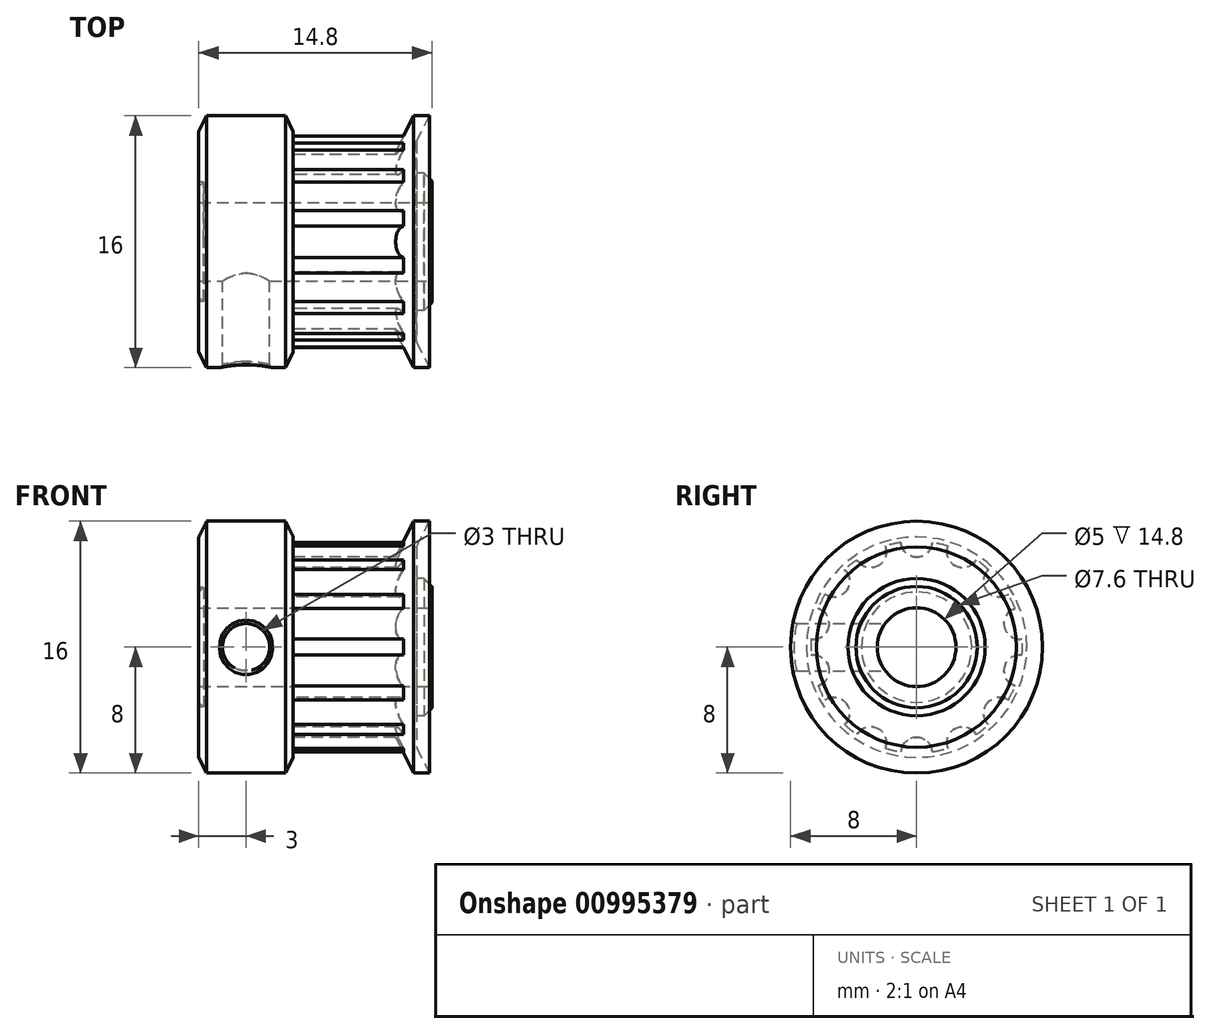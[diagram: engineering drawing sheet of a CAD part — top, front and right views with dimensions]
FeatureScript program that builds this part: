
annotation { "Feature Type Name" : "Feature", "Feature Type Description" : "" }
export const myFeature = defineFeature(function(context is Context, id is Id, definition is map)
    precondition{}
    {
        {
            var Q0;
            Q0=qCreatedBy(makeId("Front.planeOp"),FACE);
            var sketch = newSketch(context, id + "F0", { "sketchPlane" : qUnion([Q0])});
            skLineSegment(sketch, "E0", {"start": v(0, 7) * mm, "end": v(0, 3.8) * mm, "construction": true});
            skLineSegment(sketch, "E1", {"start": v(0, 0) * mm, "end": v(14.8, 0) * mm, "construction": true});
            skLineSegment(sketch, "E2", {"start": v(0, 7) * mm, "end": v(0, 3.9) * mm});
            skLineSegment(sketch, "E3", {"start": v(0.5, 8) * mm, "end": v(5.5, 8) * mm});
            skLineSegment(sketch, "E4", {"start": v(5.5, 8) * mm, "end": v(6, 7) * mm});
            skLineSegment(sketch, "E5", {"start": v(6, 7) * mm, "end": v(6, 6.72) * mm});
            skLineSegment(sketch, "E6", {"start": v(6, 6.72) * mm, "end": v(13, 6.72) * mm});
            skLineSegment(sketch, "E7", {"start": v(13, 6.72) * mm, "end": v(13.64, 8) * mm});
            skLineSegment(sketch, "E8", {"start": v(13.64, 8) * mm, "end": v(14.64, 8) * mm});
            skPoint(sketch, "E9.endSnap0", {"position": v(14.14, 8) * mm});
            skLineSegment(sketch, "E10", {"start": v(0, 7) * mm, "end": v(0.5, 8) * mm});
            skLineSegment(sketch, "E11", {"start": v(0.1, 3.8) * mm, "end": v(0.3, 3.8) * mm});
            skLineSegment(sketch, "E12", {"start": v(0.3, 3.8) * mm, "end": v(0, 3.5) * mm});
            skLineSegment(sketch, "E13.trimOffspring", {"start": v(0, 3.5) * mm, "end": v(0, 0) * mm, "construction": true});
            skLineSegment(sketch, "E14.trimOffspring", {"start": v(0, 3.5) * mm, "end": v(0, 0) * mm});
            skPoint(sketch, "E15.visualSharp", {"position": v(14.8, 0) * mm});
            skPoint(sketch, "E16.visualSharp", {"position": v(0, 3.8) * mm});
            skArc(sketch, "E16.filletArc", {"start": v(0, 3.9) * mm, "mid": v(0.03, 3.83) * mm, "end": v(0.1, 3.8) * mm});
            skLineSegment(sketch, "E17", {"start": v(13.82, 4.35) * mm, "end": v(14.3, 4.35) * mm});
            skLineSegment(sketch, "E18", {"start": v(14.8, 3.85) * mm, "end": v(14.8, 0) * mm});
            skLineSegment(sketch, "E19", {"start": v(14.3, 4.35) * mm, "end": v(14.8, 3.85) * mm});
            skPoint(sketch, "E20.orphan", {"position": v(14.8, 4.35) * mm});
            skLineSegment(sketch, "E21", {"start": v(14.64, 8) * mm, "end": v(13.82, 6.35) * mm});
            skLineSegment(sketch, "E22", {"start": v(13.82, 6.35) * mm, "end": v(13.82, 4.35) * mm});
            skPoint(sketch, "E23.orphan", {"position": v(14.14, 4.35) * mm});
            skLineSegment(sketch, "E24", {"start": v(0, 0) * mm, "end": v(14.8, 0) * mm});
            skSolve(sketch);
        }
        {
            var Q0;
            Q0 = qSketchRegion(id + "F0", true);
            var Q1;
            Q1=sQuery(id+"F0.wireOp",EDGE,"E24");
            revolve(context, id + "F1", {"surfaceOperationType" : NewSurfaceOperationType.NEW, "entities" : qUnion([Q0]), "axis" : qUnion([Q1]), "revolveType" : RevolveType.FULL});
        }
        {
            var Q0;
            Q0=makeQuery(id+"F1.opRevolve","SWEPT_FACE",FACE,{"disambiguationData":[OSD([sQuery(id+"F0.wireOp",EDGE,"E18")])]});
            var sketch = newSketch(context, id + "F2", { "sketchPlane" : qUnion([Q0])});
            skSolve(sketch);
        }
        {
            var Q0;
            Q0=makeQuery(id+"F2.imprint","IMPRINT",FACE,{"disambiguationData":[TD([[makeQuery(id+"F2.imprint","IMPRINT",EDGE,{"derivedFrom":makeQuery(id+"F1.opRevolve","SWEPT_EDGE",EDGE,{"disambiguationData":[OSD([sQuery(id+"F0.wireOp",EDGE,"E18"),sQuery(id+"F0.wireOp",EDGE,"E19")])]})}),-1.0]])]});
            var sketch = newSketch(context, id + "F3", { "sketchPlane" : qUnion([Q0])});
            skCircle(sketch, "E25", {"center": v(0, 0) * mm, "radius": 2.5 * mm});
            skSolve(sketch);
        }
        {
            var Q0;
            Q0 = qSketchRegion(id + "F3", true);
            extrude(context, id + "F4", {"entities" : qUnion([Q0]), "operationType" : NewBodyOperationType.REMOVE, "endBound" : BoundingType.THROUGH_ALL, "oppositeDirection" : true, "depth" : 25 * mm, "offsetDistance" : 25 * mm});
        }
        {
            var Q0;
            Q0=makeQuery(id+"F1.opRevolve","SWEPT_FACE",FACE,{"disambiguationData":[OSD([sQuery(id+"F0.wireOp",EDGE,"E5")])]});
            var sketch = newSketch(context, id + "F5", { "sketchPlane" : qUnion([Q0])});
            skLineSegment(sketch, "E26", {"start": v(0, 0) * mm, "end": v(0, 6.72) * mm, "construction": true});
            skSolve(sketch);
        }
        {
            var Q0;
            {var subQ0=sQuery(id+"F0.wireOp",EDGE,"E5");Q0=makeQuery(id+"F5.imprint","IMPRINT",FACE,{"disambiguationData":[TD([[makeQuery(id+"F5.imprint","IMPRINT",EDGE,{"derivedFrom":makeQuery(id+"F1.opRevolve","SWEPT_EDGE",EDGE,{"disambiguationData":[OSD([sQuery(id+"F0.wireOp",EDGE,"E4"),subQ0])]})}),-1.0]])]});}
            var sketch = newSketch(context, id + "F6", { "sketchPlane" : qUnion([Q0])});
            skCircle(sketch, "E27", {"center": v(0, 6.72) * mm, "radius": 1 * mm});
            skCircle(sketch, "E28.1.0", {"center": v(-2.92, 6.05) * mm, "radius": 1 * mm});
            skCircle(sketch, "E28.2.0", {"center": v(-5.25, 4.19) * mm, "radius": 1 * mm});
            skCircle(sketch, "E28.3.0", {"center": v(-6.55, 1.5) * mm, "radius": 1 * mm});
            skCircle(sketch, "E28.4.0", {"center": v(-6.55, -1.5) * mm, "radius": 1 * mm});
            skCircle(sketch, "E28.5.0", {"center": v(-5.25, -4.19) * mm, "radius": 1 * mm});
            skCircle(sketch, "E28.6.0", {"center": v(-2.92, -6.05) * mm, "radius": 1 * mm});
            skCircle(sketch, "E28.7.0", {"center": v(0, -6.72) * mm, "radius": 1 * mm});
            skCircle(sketch, "E28.8.0", {"center": v(2.92, -6.05) * mm, "radius": 1 * mm});
            skCircle(sketch, "E28.9.0", {"center": v(5.25, -4.19) * mm, "radius": 1 * mm});
            skCircle(sketch, "E28.10.0", {"center": v(6.55, -1.5) * mm, "radius": 1 * mm});
            skCircle(sketch, "E28.11.0", {"center": v(6.55, 1.5) * mm, "radius": 1 * mm});
            skCircle(sketch, "E28.12.0", {"center": v(5.25, 4.19) * mm, "radius": 1 * mm});
            skCircle(sketch, "E28.13.0", {"center": v(2.92, 6.05) * mm, "radius": 1 * mm});
            skPoint(sketch, "E28.center", {"position": v(0, 0) * mm});
            skSolve(sketch);
        }
        {
            var Q0;
            Q0 = qSketchRegion(id + "F6", true);
            var Q1;
            Q1=makeQuery(id+"F1.opRevolve","SWEPT_FACE",FACE,{"disambiguationData":[OSD([sQuery(id+"F0.wireOp",EDGE,"E7")])]});
            extrude(context, id + "F7", {"entities" : qUnion([Q0]), "operationType" : NewBodyOperationType.REMOVE, "endBound" : BoundingType.UP_TO_SURFACE, "depth" : 25 * mm, "endBoundEntityFace" : qUnion([Q1]), "offsetDistance" : 25 * mm});
        }
        {
            var Q0;
            Q0=qCreatedBy(makeId("Front.planeOp"),FACE);
            var sketch = newSketch(context, id + "F8", { "sketchPlane" : qUnion([Q0])});
            skLineSegment(sketch, "E29", {"start": v(0, 0) * mm, "end": v(6.13, 0) * mm, "construction": true});
            skCircle(sketch, "E30", {"center": v(3, 0) * mm, "radius": 1.5 * mm});
            skSolve(sketch);
        }
        {
            var Q0;
            Q0 = qSketchRegion(id + "F8", true);
            extrude(context, id + "F9", {"entities" : qUnion([Q0]), "operationType" : NewBodyOperationType.REMOVE, "depth" : 25 * mm, "offsetDistance" : 25 * mm});
        }
        {
            var Q0;
            Q0=makeQuery(id+"F9.boolean.opBoolean","INTERSECT",EDGE,{"derivedFrom":[makeQuery(id+"F1.opRevolve","SWEPT_FACE",FACE,{"disambiguationData":[OSD([sQuery(id+"F0.wireOp",EDGE,"E3")])]}),makeQuery(id+"F9.opExtrude","SWEPT_FACE",FACE,{"disambiguationData":[OSD([sQuery(id+"F8.wireOp",EDGE,"E30")])]})]});
            fillet(context, id + "F10", {"entities" : qUnion([Q0]), "radius" : .2 * mm, "tangentPropagation" : true, "allowEdgeOverflow" : false});
        }
    });
